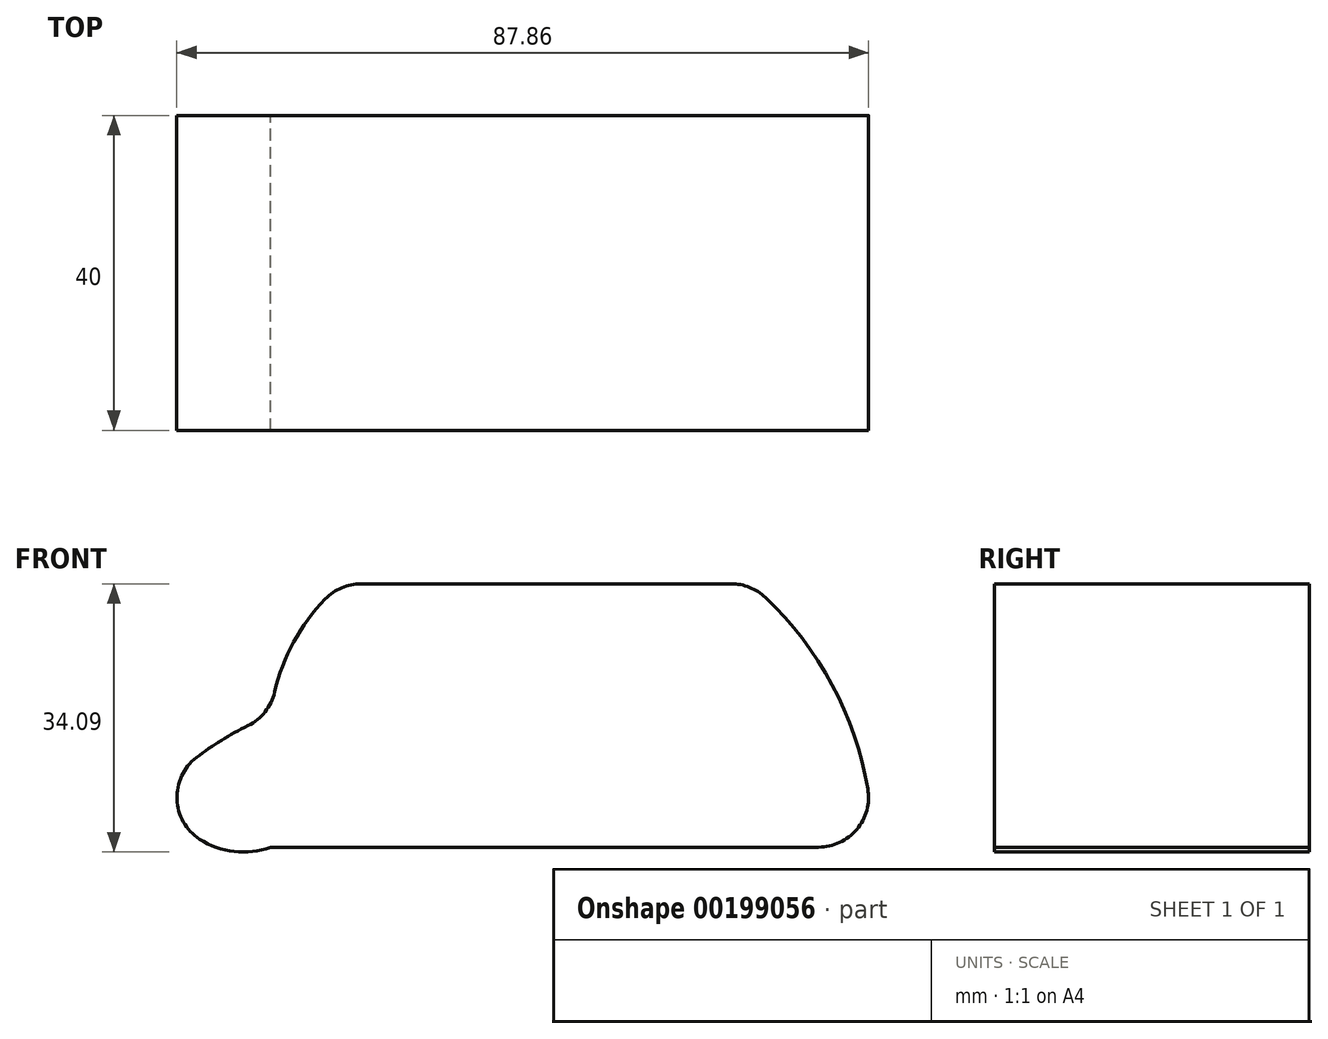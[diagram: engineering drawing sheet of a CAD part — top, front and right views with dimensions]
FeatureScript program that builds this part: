
annotation { "Feature Type Name" : "Feature", "Feature Type Description" : "" }
export const myFeature = defineFeature(function(context is Context, id is Id, definition is map)
    precondition{}
    {
        {
            var Q0;
            Q0=qCreatedBy(makeId("Front.planeOp"),FACE);
            var sketch = newSketch(context, id + "F0", { "sketchPlane" : qUnion([Q0])});
            skLineSegment(sketch, "E0.bottom", {"start": v(20.24, 16.73) * mm, "end": v(-26.74, 16.73) * mm});
            skLineSegment(sketch, "E0.top", {"start": v(31.35, -16.73) * mm, "end": v(-38.24, -16.73) * mm});
            skPoint(sketch, "E0.middle", {"position": v(0, 0) * mm});
            skArc(sketch, "E1", {"start": v(-31.3, 14.8) * mm, "mid": v(-35.32, 9.32) * mm, "end": v(-37.74, 2.98) * mm});
            skPoint(sketch, "E2.orphan", {"position": v(-38.24, 16.73) * mm});
            skPoint(sketch, "E3.visualSharp", {"position": v(-29.21, 16.73) * mm});
            skArc(sketch, "E3.filletArc", {"start": v(-26.74, 16.73) * mm, "mid": v(-29.22, 16.22) * mm, "end": v(-31.3, 14.8) * mm});
            skArc(sketch, "E4", {"start": v(37.6, -9.3) * mm, "mid": v(33.07, 3.9) * mm, "end": v(24.6, 14.99) * mm});
            skPoint(sketch, "E0.left.start.orphan", {"position": v(38.24, 16.73) * mm});
            skPoint(sketch, "E5.visualSharp", {"position": v(38.24, -16.73) * mm});
            skArc(sketch, "E5.filletArc", {"start": v(31.35, -16.73) * mm, "mid": v(36.2, -14.47) * mm, "end": v(37.6, -9.3) * mm});
            skPoint(sketch, "E6.visualSharp", {"position": v(22.66, 16.73) * mm});
            skArc(sketch, "E6.filletArc", {"start": v(24.6, 14.99) * mm, "mid": v(22.6, 16.28) * mm, "end": v(20.24, 16.73) * mm});
            skArc(sketch, "E7", {"start": v(-41.11, -1.28) * mm, "mid": v(-44.5, -3.16) * mm, "end": v(-47.67, -5.35) * mm});
            skArc(sketch, "E8", {"start": v(-47.28, -15.71) * mm, "mid": v(-42.88, -17.3) * mm, "end": v(-38.24, -16.73) * mm});
            skPoint(sketch, "E9.visualSharp", {"position": v(-38.24, 0) * mm});
            skArc(sketch, "E9.filletArc", {"start": v(-41.11, -1.28) * mm, "mid": v(-38.95, 0.47) * mm, "end": v(-37.74, 2.98) * mm});
            skPoint(sketch, "E10.visualSharp", {"position": v(-51.73, -8.93) * mm});
            skArc(sketch, "E10.filletArc", {"start": v(-47.67, -5.35) * mm, "mid": v(-50.16, -10.64) * mm, "end": v(-47.28, -15.71) * mm});
            skSolve(sketch);
        }
        {
            var Q0;
            Q0 = qSketchRegion(id + "F0", true);
            extrude(context, id + "F1", {"entities" : qUnion([Q0]), "depth" : 40 * mm});
        }
    });
